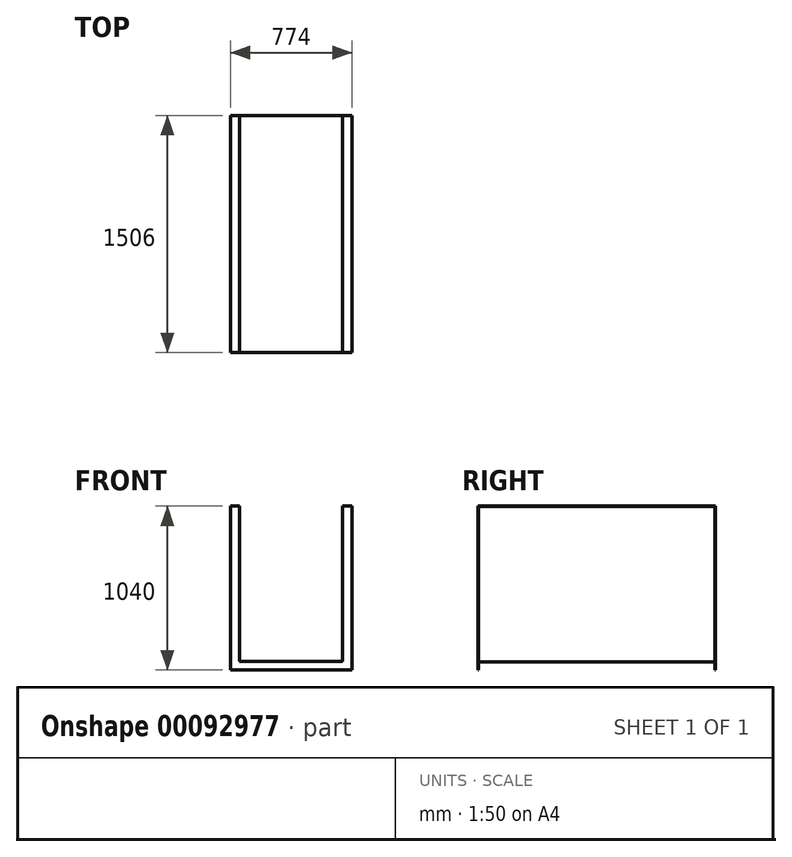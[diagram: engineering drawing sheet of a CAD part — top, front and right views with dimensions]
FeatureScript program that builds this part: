
annotation { "Feature Type Name" : "Feature", "Feature Type Description" : "" }
export const myFeature = defineFeature(function(context is Context, id is Id, definition is map)
    precondition{}
    {
        {
            var Q0;
            Q0=qCreatedBy(makeId("Front.planeOp"),FACE);
            var sketch = newSketch(context, id + "F0", { "sketchPlane" : qUnion([Q0])});
            skLineSegment(sketch, "E0", {"start": v(-330, 990) * mm, "end": v(-330, 0) * mm});
            skLineSegment(sketch, "E1", {"start": v(-330, 0) * mm, "end": v(0, 0) * mm});
            skLineSegment(sketch, "E2", {"start": v(0, 0) * mm, "end": v(330, 0) * mm});
            skLineSegment(sketch, "E3", {"start": v(330, 0) * mm, "end": v(330, 990) * mm});
            skLineSegment(sketch, "E4", {"start": v(330, 990) * mm, "end": v(-330, 990) * mm});
            skLineSegment(sketch, "E5", {"start": v(-200.03, 0) * mm, "end": v(-296.75, 0) * mm, "construction": true});
            skSolve(sketch);
        }
        {
            var Q0;
            Q0=makeQuery(id+"F0.imprint","IMPRINT",FACE,{"disambiguationData":[TD([[makeQuery(id+"F0.imprint","IMPRINT",EDGE,{"derivedFrom":sQuery(id+"F0.wireOp",EDGE,"E0")}),1.0]])]});
            var Q1;
            Q1=sQuery(id+"F0.wireOp",EDGE,"E0");
            var Q2;
            Q2=sQuery(id+"F0.wireOp",EDGE,"E1");
            var Q3;
            Q3=sQuery(id+"F0.wireOp",EDGE,"E2");
            var Q4;
            Q4=sQuery(id+"F0.wireOp",EDGE,"E3");
            extrude(context, id + "F1", {"entities" : qUnion([Q0]), "surfaceEntities" : qUnion([Q1, Q2, Q3, Q4]), "depth" : 1500 * mm});
        }
        {
            var Q0;
            Q0=makeQuery(id+"F1.opExtrude","CAP_FACE",FACE,{"disambiguationData":[OSD([sQuery(id+"F0.wireOp",EDGE,"E0"),sQuery(id+"F0.wireOp",EDGE,"E1"),sQuery(id+"F0.wireOp",EDGE,"E2"),sQuery(id+"F0.wireOp",EDGE,"E3"),sQuery(id+"F0.wireOp",EDGE,"E4")])],"isStart":false});
            var Q1;
            Q1=makeQuery(id+"F1.opExtrude","SWEPT_FACE",FACE,{"disambiguationData":[OSD([sQuery(id+"F0.wireOp",EDGE,"E4")])]});
            var Q2;
            Q2=makeQuery(id+"F1.opExtrude","CAP_FACE",FACE,{"disambiguationData":[OSD([sQuery(id+"F0.wireOp",EDGE,"E0"),sQuery(id+"F0.wireOp",EDGE,"E1"),sQuery(id+"F0.wireOp",EDGE,"E2"),sQuery(id+"F0.wireOp",EDGE,"E3"),sQuery(id+"F0.wireOp",EDGE,"E4")])],"isStart":true});
            shell(context, id + "F2", {"entities" : qUnion([Q0, Q1, Q2]), "thickness" : 3 * mm});
        }
        {
            var Q0;
            Q0=makeQuery(id+"F1.opExtrude","SWEPT_FACE",FACE,{"disambiguationData":[OSD([sQuery(id+"F0.wireOp",EDGE,"E4")])]});
            var sketch = newSketch(context, id + "F3", { "sketchPlane" : qUnion([Q0])});
            skLineSegment(sketch, "E6", {"start": v(-387, 0) * mm, "end": v(-387, -1500) * mm});
            skLineSegment(sketch, "E7", {"start": v(387, 0) * mm, "end": v(387, -1500) * mm});
            skLineSegment(sketch, "E8", {"start": v(-327, 0) * mm, "end": v(-327, -1500) * mm});
            skLineSegment(sketch, "E9", {"start": v(-327, -1500) * mm, "end": v(-387, -1500) * mm});
            skLineSegment(sketch, "E10", {"start": v(-327, 0) * mm, "end": v(-387, 0) * mm});
            skLineSegment(sketch, "E11", {"start": v(327, 0) * mm, "end": v(387, 0) * mm});
            skLineSegment(sketch, "E12", {"start": v(327, 0) * mm, "end": v(327, -1500) * mm});
            skLineSegment(sketch, "E13", {"start": v(327, -1500) * mm, "end": v(387, -1500) * mm});
            skSolve(sketch);
        }
        {
            var Q0;
            Q0=qSketchRegion(id+"F3",true);
            extrude(context, id + "F4", {"entities" : qUnion([Q0]), "operationType" : NewBodyOperationType.ADD, "oppositeDirection" : true, "depth" : 3 * mm});
        }
        {
            var Q0;
            Q0=makeQuery(id+"F4.boolean.opBoolean","MERGE",FACE,{"derivedFrom":[makeQuery(id+"F1.opExtrude","CAP_FACE",FACE,{"disambiguationData":[OSD([sQuery(id+"F0.wireOp",EDGE,"E0"),sQuery(id+"F0.wireOp",EDGE,"E1"),sQuery(id+"F0.wireOp",EDGE,"E2"),sQuery(id+"F0.wireOp",EDGE,"E3"),sQuery(id+"F0.wireOp",EDGE,"E4")])],"isStart":true}),makeQuery(id+"F4.opExtrude","SWEPT_FACE",FACE,{"disambiguationData":[OSD([sQuery(id+"F3.wireOp",EDGE,"E10")])]}),makeQuery(id+"F4.opExtrude","SWEPT_FACE",FACE,{"disambiguationData":[OSD([sQuery(id+"F3.wireOp",EDGE,"E11")])]})]});
            var sketch = newSketch(context, id + "F5", { "sketchPlane" : qUnion([Q0])});
            skLineSegment(sketch, "E14.0", {"start": v(327, 990) * mm, "end": v(387, 990) * mm});
            skLineSegment(sketch, "E15.0", {"start": v(327, 990) * mm, "end": v(327, 3) * mm});
            skLineSegment(sketch, "E16.0", {"start": v(327, 3) * mm, "end": v(327, 3) * mm});
            skLineSegment(sketch, "E17.0", {"start": v(327, 3) * mm, "end": v(-327, 3) * mm});
            skLineSegment(sketch, "E18.0", {"start": v(-327, 3) * mm, "end": v(-327, 990) * mm});
            skLineSegment(sketch, "E19.0", {"start": v(-387, 990) * mm, "end": v(-327, 990) * mm});
            skLineSegment(sketch, "E20", {"start": v(387, 990) * mm, "end": v(387, -50) * mm});
            skLineSegment(sketch, "E21", {"start": v(-387, 990) * mm, "end": v(-387, -50) * mm});
            skLineSegment(sketch, "E22", {"start": v(-387, -50) * mm, "end": v(-75.37, -50) * mm});
            skLineSegment(sketch, "E23", {"start": v(387, -50) * mm, "end": v(-75.37, -50) * mm});
            skSolve(sketch);
        }
        {
            var Q0;
            Q0=qSketchRegion(id+"F5",true);
            extrude(context, id + "F6", {"entities" : qUnion([Q0]), "operationType" : NewBodyOperationType.ADD, "depth" : 3 * mm});
        }
        {
            var Q0;
            Q0=makeQuery(id+"F4.boolean.opBoolean","MERGE",FACE,{"derivedFrom":[makeQuery(id+"F1.opExtrude","CAP_FACE",FACE,{"disambiguationData":[OSD([sQuery(id+"F0.wireOp",EDGE,"E0"),sQuery(id+"F0.wireOp",EDGE,"E1"),sQuery(id+"F0.wireOp",EDGE,"E2"),sQuery(id+"F0.wireOp",EDGE,"E3"),sQuery(id+"F0.wireOp",EDGE,"E4")])],"isStart":false}),makeQuery(id+"F4.opExtrude","SWEPT_FACE",FACE,{"disambiguationData":[OSD([sQuery(id+"F3.wireOp",EDGE,"E9")])]}),makeQuery(id+"F4.opExtrude","SWEPT_FACE",FACE,{"disambiguationData":[OSD([sQuery(id+"F3.wireOp",EDGE,"E13")])]})]});
            var sketch = newSketch(context, id + "F7", { "sketchPlane" : qUnion([Q0])});
            skLineSegment(sketch, "E24.0", {"start": v(387, 990) * mm, "end": v(327, 990) * mm});
            skLineSegment(sketch, "E25.0", {"start": v(327, 3) * mm, "end": v(327, 990) * mm});
            skLineSegment(sketch, "E26.0", {"start": v(-327, 3) * mm, "end": v(327, 3) * mm});
            skLineSegment(sketch, "E27.0", {"start": v(-327, 3) * mm, "end": v(-327, 3) * mm});
            skLineSegment(sketch, "E28.0", {"start": v(-327, 990) * mm, "end": v(-387, 990) * mm});
            skLineSegment(sketch, "E29.0", {"start": v(-327, 990) * mm, "end": v(-327, 3) * mm});
            skLineSegment(sketch, "E30", {"start": v(-387, 990) * mm, "end": v(-387, -50) * mm});
            skLineSegment(sketch, "E31", {"start": v(387, 990) * mm, "end": v(387, -50) * mm});
            skLineSegment(sketch, "E32", {"start": v(-387, -50) * mm, "end": v(-70.36, -50) * mm});
            skLineSegment(sketch, "E33", {"start": v(387, -50) * mm, "end": v(-70.36, -50) * mm});
            skSolve(sketch);
        }
        {
            var Q0;
            Q0=qSketchRegion(id+"F7",true);
            extrude(context, id + "F8", {"entities" : qUnion([Q0]), "operationType" : NewBodyOperationType.ADD, "depth" : 3 * mm});
        }
    });
